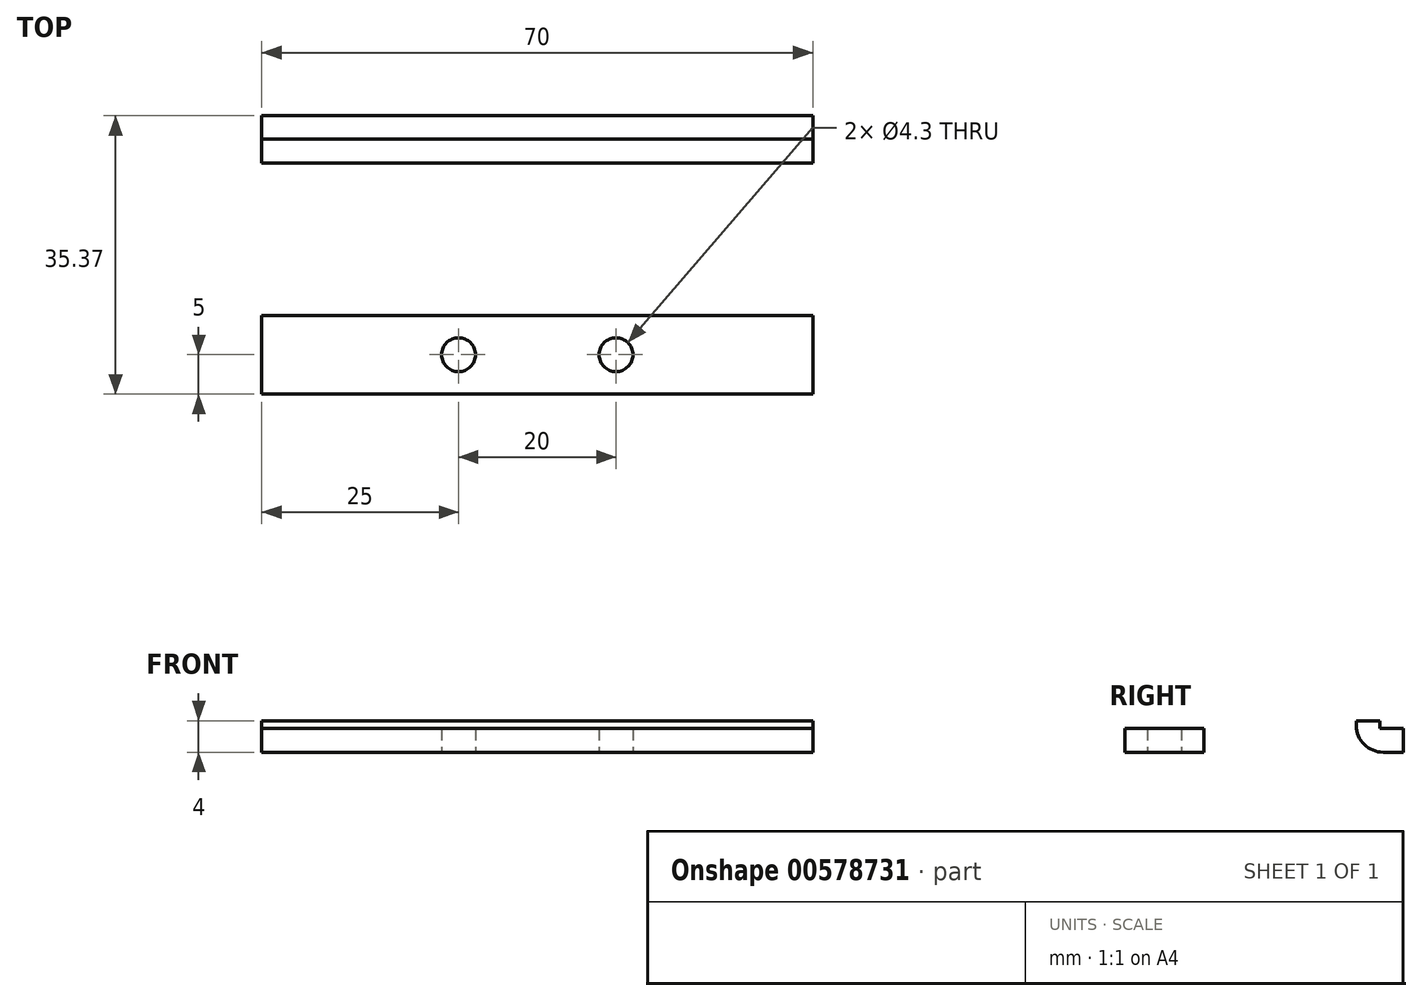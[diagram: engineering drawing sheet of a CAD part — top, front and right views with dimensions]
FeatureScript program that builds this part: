
annotation { "Feature Type Name" : "Feature", "Feature Type Description" : "" }
export const myFeature = defineFeature(function(context is Context, id is Id, definition is map)
    precondition{}
    {
        {
            var Q0;
            Q0=qCreatedBy(makeId("Top.planeOp"),FACE);
            var sketch = newSketch(context, id + "F0", { "sketchPlane" : qUnion([Q0])});
            skLineSegment(sketch, "E0.bottom", {"start": v(35, -5) * mm, "end": v(-35, -5) * mm});
            skLineSegment(sketch, "E0.top", {"start": v(35, 5) * mm, "end": v(-35, 5) * mm});
            skLineSegment(sketch, "E0.left", {"start": v(35, -5) * mm, "end": v(35, 5) * mm});
            skLineSegment(sketch, "E0.right", {"start": v(-35, -5) * mm, "end": v(-35, 5) * mm});
            skPoint(sketch, "E0.middle", {"position": v(0, 0) * mm});
            skLineSegment(sketch, "E1.bottom", {"start": v(35, 24.37) * mm, "end": v(-35, 24.37) * mm});
            skLineSegment(sketch, "E1.top", {"start": v(35, 30.37) * mm, "end": v(-35, 30.37) * mm});
            skLineSegment(sketch, "E1.left", {"start": v(35, 24.37) * mm, "end": v(35, 30.37) * mm});
            skLineSegment(sketch, "E1.right", {"start": v(-35, 24.37) * mm, "end": v(-35, 30.37) * mm});
            skPoint(sketch, "E1.middle", {"position": v(0, 27.37) * mm});
            skLineSegment(sketch, "E2", {"start": v(-35, 27.37) * mm, "end": v(35, 27.37) * mm});
            skCircle(sketch, "E3", {"center": v(10, 0) * mm, "radius": 2.15 * mm});
            skCircle(sketch, "E4.MirrorC", {"center": v(-10, 0) * mm, "radius": 2.15 * mm});
            skSolve(sketch);
        }
        {
            var Q0;
            Q0=makeQuery(id+"F0.imprint","IMPRINT",FACE,{"disambiguationData":[TD([[makeQuery(id+"F0.imprint","IMPRINT",EDGE,{"derivedFrom":sQuery(id+"F0.wireOp",EDGE,"E0.bottom")}),-1.0]])]});
            extrude(context, id + "F1", {"entities" : qUnion([Q0]), "depth" : 3 * mm, "offsetDistance" : 25 * mm});
        }
        {
            var Q0;
            {var subQ0=sQuery(id+"F0.wireOp",EDGE,"E1.bottom");Q0=makeQuery(id+"F0.imprint","IMPRINT",FACE,{"disambiguationData":[TD([[makeQuery(id+"F0.imprint","IMPRINT",EDGE,{"derivedFrom":subQ0}),-1.0]])]});}
            var Q1;
            {var subQ0=sQuery(id+"F0.wireOp",EDGE,"E1.top");Q1=makeQuery(id+"F0.imprint","IMPRINT",FACE,{"disambiguationData":[TD([[makeQuery(id+"F0.imprint","IMPRINT",EDGE,{"derivedFrom":subQ0}),1.0]])]});}
            extrude(context, id + "F2", {"entities" : qUnion([Q0, Q1]), "depth" : 3 * mm, "offsetDistance" : 25 * mm});
        }
        {
            var Q0;
            {var subQ0=sQuery(id+"F0.wireOp",EDGE,"E1.bottom");Q0=makeQuery(id+"F0.imprint","IMPRINT",FACE,{"disambiguationData":[TD([[makeQuery(id+"F0.imprint","IMPRINT",EDGE,{"derivedFrom":subQ0}),-1.0]])]});}
            extrude(context, id + "F3", {"entities" : qUnion([Q0]), "operationType" : NewBodyOperationType.ADD, "depth" : 4 * mm, "offsetDistance" : 25 * mm});
        }
        {
            var Q0;
            Q0=makeQuery(id+"F2.opExtrude","CAP_EDGE",EDGE,{"disambiguationData":[OSD([sQuery(id+"F0.wireOp",EDGE,"E1.bottom")])],"isStart":true});
            fillet(context, id + "F4", {"entities" : qUnion([Q0]), "radius" : 3.4 * mm, "tangentPropagation" : true, "allowEdgeOverflow" : false});
        }
    });
